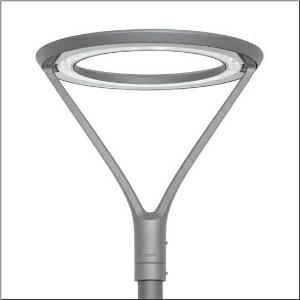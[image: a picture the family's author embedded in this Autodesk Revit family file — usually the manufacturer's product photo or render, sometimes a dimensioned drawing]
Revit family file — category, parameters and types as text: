
# Revit family: dl_r__20_led___pl1_2s_5xa51283ns008_aa8a
name_source: partatom
category: Lighting Fixtures
units: mm (PartAtom-declared; Revit-internal decimal feet)

## family parameters
Cut with Voids When Loaded = No
Host = Face
Light Source = No
Part Type = Normal
Room Calculation Point = No
Round Connector Dimension = Use Diameter
Shared = No

## types (1)
- --- (1 x LED 4000K / CRI = 80 (unbekannt), 3030 lm, 4000K)
    Apparent Load = 27 VA
    CIE Flux Codes = 34 78 98 100 100
    Color Rendering = 80
    Color Temperature = 4000K
    Default Elevation = 1800 mm
    Description = DL® 20 LED, mast luminaire, primary light control with reflector, highly specular, primary optical cover: cover, of toughened safety glass of clear glass with excellent transmission level, light distribution: PL1.2s, light emission: direct distribution, primary light characteristic: symmetric, installation type: post-top, LED High Power LED, rated luminous flux: 3.030 lm, light colour: 840, colour temperature: 4000K, control gear: ECG Plus, control: overheat protection, power reduction, digital communication interface, constant luminous flux control, time-dependent luminous flux control, flexible luminous flux parameterisation, electronic power reduction, mains connection: 220..240V, 50/60Hz, connection cable pre-assembled, cable length: 5 m, start of lifetime: 27 W, end of lifetime: 28 W, reduction: 14 W, luminaire housing, upper part, of cast aluminium, powder-coated, Siteco® metallic grey (DB 702S), diameter: 690 mm, height: 690mm, spigot size: 76mm (post-top), luminaire housing, of cast aluminium, powder-coated, Siteco® metallic grey (DB 702S), protection rating (complete): IP66, insulation class (complete): insulation class II (safety insulation), certification: CE, ENEC, VDE, impact resistance: IK08, permissible ambient temperature for indoor applications: -25..+35°C, standard-compliant lighting for roads and squares, packaging unit: 1 piece

Light Distribution: PL1.2s
    Height = 690 mm
    Lamp = 1 x LED 4000K / CRI >= 80 (unbekannt)
    Lamp Light Flux = 3030 lm
    Lamp count = 1
    Length = 690 mm
    Luminous efficacy = 111 lm/W
    Manufacturer = Siteco
    ModVariant = No
    Model = 5XA51283NS008
    Number of Poles = 1
    OnlyDefault = Yes
    Power Factor = 1
    Product Name = DL® 20 LED | PL1.2s
    Product group = mast luminaire | pylon top
    ProductGroupID = 6100
    Protection Class = Protection class II
    Protection Degree = IP 66
    RLX_Detail_Level = 1
    RlxData = <blob elided: 203465 chars, md5=0a58ceac>
    Socket = socket
    Standby Power = 0 W
    System Light Flux = 3030 lm
    System Power = 27 W
    Type Comments = factory setting: luminous flux: 100 % | dim-lin: 254 | 358 mA
    Type Image = l_1006001.jpg
    URL = http://relux.com
    VarID = @adj_141563
    Voltage = 0 V
    Weight = 0.00 kg
    Width = 0 mm  [stored 0 ft]

note: [stored X ft] marks values corroborated as IEEE doubles in the binary element streams (Revit-internal decimal feet)

## geometry (parser evidence)
native form markers: Blend x4, Sweep x9
no freeform markers — native parametric forms only
